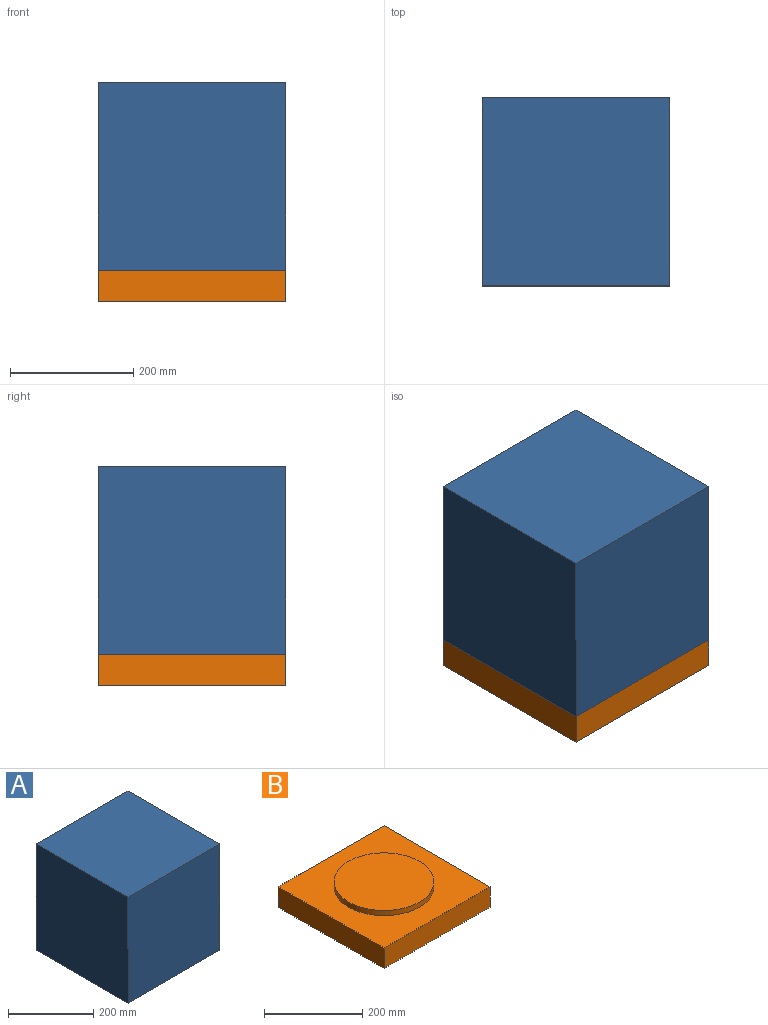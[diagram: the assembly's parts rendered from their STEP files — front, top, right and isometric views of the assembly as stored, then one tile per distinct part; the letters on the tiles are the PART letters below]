
ASSEMBLY  parts=2 mates=2
PART A: 11 faces, bbox 304.8x304.8x304.8 mm
  f0: plane 304.8x304.8mm, normal (0,0,-1), area 7580.6mm2, adj f1,f2,f4,f5,f6,f7,f9,f10
  f1: plane 304.8x304.8mm, normal (-1,0,0), area 92903mm2, adj f0,f3,f4,f5
  f2: plane 304.8x304.8mm, normal (1,0,0), area 92903mm2, adj f0,f3,f4,f5
  f3: plane 304.8x304.8mm, normal (0,0,1), area 92903mm2, adj f1,f2,f4,f5
  f4: plane 304.8x304.8mm, normal (0,-1,0), area 92903mm2, adj f0,f1,f2,f3
  f5: plane 304.8x304.8mm, normal (0,1,0), area 92903mm2, adj f0,f1,f2,f3
  f6: plane 298.45x292.1mm, normal (1,0,0), area 87177.2mm2, adj f0,f8,f9,f10
  f7: plane 298.45x292.1mm, normal (-1,0,0), area 87177.2mm2, adj f0,f8,f9,f10
  f8: plane 292.1x292.1mm, normal (0,0,-1), area 85322.4mm2, adj f6,f7,f9,f10
  f9: plane 298.45x292.1mm, normal (0,1,0), area 87177.2mm2, adj f0,f6,f7,f8
  f10: plane 298.45x292.1mm, normal (0,-1,0), area 87177.2mm2, adj f0,f6,f7,f8
PART B: 8 faces, bbox 304.8x304.8x63.5 mm
  f0: plane 304.8x50.8mm, normal (-1,0,0), area 15483.8mm2, adj f1,f3,f4,f5
  f1: plane 304.8x50.8mm, normal (0,-1,0), area 15483.8mm2, adj f0,f2,f4,f5
  f2: plane 304.8x50.8mm, normal (1,0,0), area 15483.8mm2, adj f1,f3,f4,f5
  f3: plane 304.8x50.8mm, normal (0,1,0), area 15483.8mm2, adj f0,f2,f4,f5
  f4: plane 304.8x304.8mm, normal (0,0,1), area 60473.8mm2, adj f0,f1,f2,f3,f6
  f5: plane 304.8x304.8mm, normal (0,0,-1), area 92903mm2, adj f0,f1,f2,f3
  f6: cylinder r=101.6mm len=203.2mm, axis (0,0,-1), area 8107.3mm2, adj f4,f7
  f7: plane 203.2x203.2mm, normal (0,0,1), area 32429.3mm2, adj f6
PLACE A t=(203.77,304.87,-437.47)mm
PLACE B t=(203.77,0.07,-488.27)mm
MATE cylindrical B.f6 <-> A.f3  axis (0,0,1) through (356.17,152.47,-424.77)mm
MATE parallel A.f3 <-> B.f6  axis (0,0,1) through (356.17,152.47,-132.67)mm
